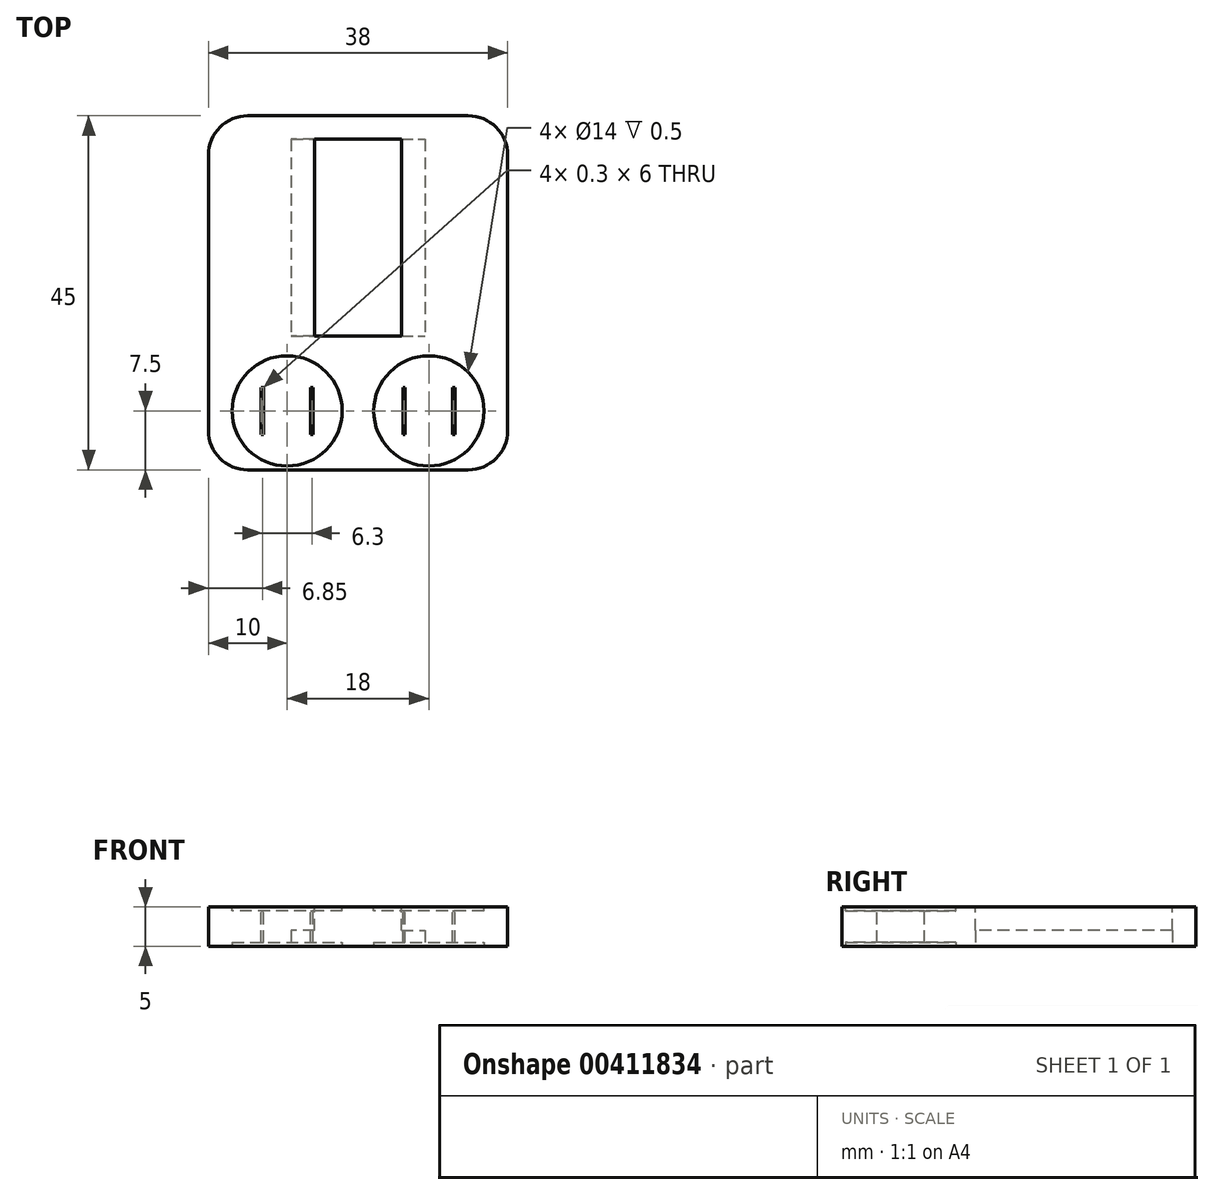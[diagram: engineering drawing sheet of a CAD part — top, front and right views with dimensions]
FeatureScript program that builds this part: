
annotation { "Feature Type Name" : "Feature", "Feature Type Description" : "" }
export const myFeature = defineFeature(function(context is Context, id is Id, definition is map)
    precondition{}
    {
        {
            var Q0;
            Q0=qCreatedBy(makeId("Top.planeOp"),FACE);
            var sketch = newSketch(context, id + "F0", { "sketchPlane" : qUnion([Q0])});
            skLineSegment(sketch, "E0.bottom", {"start": v(0, 0) * mm, "end": v(38, 0) * mm});
            skLineSegment(sketch, "E0.top", {"start": v(0, 45) * mm, "end": v(38, 45) * mm});
            skLineSegment(sketch, "E0.left", {"start": v(0, 0) * mm, "end": v(0, 45) * mm});
            skLineSegment(sketch, "E0.right", {"start": v(38, 0) * mm, "end": v(38, 45) * mm});
            skSolve(sketch);
        }
        {
            var Q0;
            Q0 = qSketchRegion(id + "F0", true);
            extrude(context, id + "F1", {"entities" : qUnion([Q0]), "depth" : 5 * mm});
        }
        {
            var Q0;
            Q0=makeQuery(id+"F1.opExtrude","CAP_FACE",FACE,{"disambiguationData":[OSD([sQuery(id+"F0.wireOp",EDGE,"E0.bottom"),sQuery(id+"F0.wireOp",EDGE,"E0.top"),sQuery(id+"F0.wireOp",EDGE,"E0.left"),sQuery(id+"F0.wireOp",EDGE,"E0.right")])],"isStart":false});
            var sketch = newSketch(context, id + "F2", { "sketchPlane" : qUnion([Q0])});
            skLineSegment(sketch, "E1.bottom", {"start": v(13.5, 42) * mm, "end": v(24.5, 42) * mm});
            skLineSegment(sketch, "E1.top", {"start": v(13.5, 17) * mm, "end": v(24.5, 17) * mm});
            skLineSegment(sketch, "E1.left", {"start": v(13.5, 42) * mm, "end": v(13.5, 17) * mm});
            skLineSegment(sketch, "E1.right", {"start": v(24.5, 42) * mm, "end": v(24.5, 17) * mm});
            skLineSegment(sketch, "E2", {"start": v(19, 45) * mm, "end": v(19, 0) * mm});
            skCircle(sketch, "E3", {"center": v(10, 7.5) * mm, "radius": 7 * mm});
            skCircle(sketch, "E4", {"center": v(28, 7.5) * mm, "radius": 7 * mm});
            skSolve(sketch);
        }
        {
            var Q0;
            Q0=makeQuery(id+"F2.imprint","IMPRINT",FACE,{"disambiguationData":[TD([[makeQuery(id+"F2.imprint","IMPRINT",EDGE,{"derivedFrom":sQuery(id+"F2.wireOp",EDGE,"E3")}),1.0]])]});
            var Q1;
            Q1=makeQuery(id+"F2.imprint","IMPRINT",FACE,{"disambiguationData":[TD([[makeQuery(id+"F2.imprint","IMPRINT",EDGE,{"derivedFrom":sQuery(id+"F2.wireOp",EDGE,"E4")}),1.0]])]});
            extrude(context, id + "F3", {"entities" : qUnion([Q0, Q1]), "operationType" : NewBodyOperationType.REMOVE, "oppositeDirection" : true, "depth" : 0.5 * mm});
        }
        {
            var Q0;
            {var subQ0=sQuery(id+"F2.wireOp",EDGE,"E1.left");Q0=makeQuery(id+"F2.imprint","IMPRINT",FACE,{"disambiguationData":[TD([[makeQuery(id+"F2.imprint","IMPRINT",EDGE,{"derivedFrom":subQ0}),1.0]])]});}
            var Q1;
            {var subQ0=sQuery(id+"F2.wireOp",EDGE,"E1.right");Q1=makeQuery(id+"F2.imprint","IMPRINT",FACE,{"disambiguationData":[TD([[makeQuery(id+"F2.imprint","IMPRINT",EDGE,{"derivedFrom":subQ0}),-1.0]])]});}
            extrude(context, id + "F4", {"entities" : qUnion([Q0, Q1]), "operationType" : NewBodyOperationType.REMOVE, "endBound" : BoundingType.THROUGH_ALL, "oppositeDirection" : true, "depth" : 25 * mm});
        }
        {
            var Q0;
            Q0=makeQuery(id+"F1.opExtrude","CAP_FACE",FACE,{"disambiguationData":[OSD([sQuery(id+"F0.wireOp",EDGE,"E0.bottom"),sQuery(id+"F0.wireOp",EDGE,"E0.top"),sQuery(id+"F0.wireOp",EDGE,"E0.left"),sQuery(id+"F0.wireOp",EDGE,"E0.right")])],"isStart":true});
            var sketch = newSketch(context, id + "F5", { "sketchPlane" : qUnion([Q0])});
            skLineSegment(sketch, "E5.bottom", {"start": v(24.5, -42) * mm, "end": v(27.5, -42) * mm});
            skLineSegment(sketch, "E5.top", {"start": v(24.5, -17) * mm, "end": v(27.5, -17) * mm});
            skLineSegment(sketch, "E5.left", {"start": v(24.5, -42) * mm, "end": v(24.5, -17) * mm});
            skLineSegment(sketch, "E5.right", {"start": v(27.5, -42) * mm, "end": v(27.5, -17) * mm});
            skLineSegment(sketch, "E6.bottom", {"start": v(13.5, -42) * mm, "end": v(10.5, -42) * mm});
            skLineSegment(sketch, "E6.top", {"start": v(13.5, -17) * mm, "end": v(10.5, -17) * mm});
            skLineSegment(sketch, "E6.left", {"start": v(13.5, -42) * mm, "end": v(13.5, -17) * mm});
            skLineSegment(sketch, "E6.right", {"start": v(10.5, -42) * mm, "end": v(10.5, -17) * mm});
            skSolve(sketch);
        }
        {
            var Q0;
            Q0 = qSketchRegion(id + "F5", true);
            extrude(context, id + "F6", {"entities" : qUnion([Q0]), "operationType" : NewBodyOperationType.REMOVE, "oppositeDirection" : true, "depth" : 2 * mm});
        }
        {
            var Q0;
            Q0=makeQuery(id+"F3.boolean.opBoolean","COPY",FACE,{"derivedFrom":makeQuery(id+"F3.opExtrude","CAP_FACE",FACE,{"disambiguationData":[OSD([sQuery(id+"F2.wireOp",EDGE,"E3")])],"isStart":false})});
            var sketch = newSketch(context, id + "F7", { "sketchPlane" : qUnion([Q0])});
            skLineSegment(sketch, "E7.bottom", {"start": v(6.7, 10.5) * mm, "end": v(7, 10.5) * mm});
            skLineSegment(sketch, "E7.top", {"start": v(6.7, 4.5) * mm, "end": v(7, 4.5) * mm});
            skLineSegment(sketch, "E7.left", {"start": v(6.7, 10.5) * mm, "end": v(6.7, 4.5) * mm});
            skLineSegment(sketch, "E7.right", {"start": v(7, 10.5) * mm, "end": v(7, 4.5) * mm});
            skLineSegment(sketch, "E8.bottom", {"start": v(13, 10.5) * mm, "end": v(13.3, 10.5) * mm});
            skLineSegment(sketch, "E8.top", {"start": v(13, 4.5) * mm, "end": v(13.3, 4.5) * mm});
            skLineSegment(sketch, "E8.left", {"start": v(13, 10.5) * mm, "end": v(13, 4.5) * mm});
            skLineSegment(sketch, "E8.right", {"start": v(13.3, 10.5) * mm, "end": v(13.3, 4.5) * mm});
            skLineSegment(sketch, "E9.bottom", {"start": v(24.7, 10.5) * mm, "end": v(25, 10.5) * mm});
            skLineSegment(sketch, "E9.top", {"start": v(24.7, 4.5) * mm, "end": v(25, 4.5) * mm});
            skLineSegment(sketch, "E9.left", {"start": v(24.7, 10.5) * mm, "end": v(24.7, 4.5) * mm});
            skLineSegment(sketch, "E9.right", {"start": v(25, 10.5) * mm, "end": v(25, 4.5) * mm});
            skLineSegment(sketch, "E10.bottom", {"start": v(31, 10.5) * mm, "end": v(31.3, 10.5) * mm});
            skLineSegment(sketch, "E10.top", {"start": v(31, 4.5) * mm, "end": v(31.3, 4.5) * mm});
            skLineSegment(sketch, "E10.left", {"start": v(31, 10.5) * mm, "end": v(31, 4.5) * mm});
            skLineSegment(sketch, "E10.right", {"start": v(31.3, 10.5) * mm, "end": v(31.3, 4.5) * mm});
            skSolve(sketch);
        }
        {
            var Q0;
            Q0 = qSketchRegion(id + "F7", true);
            extrude(context, id + "F8", {"entities" : qUnion([Q0]), "operationType" : NewBodyOperationType.REMOVE, "oppositeDirection" : true, "depth" : 5 * mm});
        }
        {
            var Q0;
            Q0=makeQuery(id+"F1.opExtrude","CAP_FACE",FACE,{"disambiguationData":[OSD([sQuery(id+"F0.wireOp",EDGE,"E0.bottom"),sQuery(id+"F0.wireOp",EDGE,"E0.top"),sQuery(id+"F0.wireOp",EDGE,"E0.left"),sQuery(id+"F0.wireOp",EDGE,"E0.right")])],"isStart":true});
            var sketch = newSketch(context, id + "F9", { "sketchPlane" : qUnion([Q0])});
            skCircle(sketch, "E11", {"center": v(28, -7.5) * mm, "radius": 7 * mm});
            skCircle(sketch, "E12", {"center": v(10, -7.5) * mm, "radius": 7 * mm});
            skSolve(sketch);
        }
        {
            var Q0;
            Q0 = qSketchRegion(id + "F9", true);
            extrude(context, id + "F10", {"entities" : qUnion([Q0]), "operationType" : NewBodyOperationType.REMOVE, "oppositeDirection" : true, "depth" : 0.5 * mm});
        }
        {
            var Q0;
            Q0=makeQuery(id+"F1.opExtrude","SWEPT_EDGE",EDGE,{"disambiguationData":[OSD([sQuery(id+"F0.wireOp",EDGE,"E0.bottom"),sQuery(id+"F0.wireOp",EDGE,"E0.left")])]});
            var Q1;
            Q1=makeQuery(id+"F1.opExtrude","SWEPT_EDGE",EDGE,{"disambiguationData":[OSD([sQuery(id+"F0.wireOp",EDGE,"E0.bottom"),sQuery(id+"F0.wireOp",EDGE,"E0.right")])]});
            var Q2;
            Q2=makeQuery(id+"F1.opExtrude","SWEPT_EDGE",EDGE,{"disambiguationData":[OSD([sQuery(id+"F0.wireOp",EDGE,"E0.top"),sQuery(id+"F0.wireOp",EDGE,"E0.right")])]});
            var Q3;
            Q3=makeQuery(id+"F1.opExtrude","SWEPT_EDGE",EDGE,{"disambiguationData":[OSD([sQuery(id+"F0.wireOp",EDGE,"E0.top"),sQuery(id+"F0.wireOp",EDGE,"E0.left")])]});
            fillet(context, id + "F11", {"entities" : qUnion([Q0, Q1, Q2, Q3]), "radius" : 5 * mm, "tangentPropagation" : true, "allowEdgeOverflow" : false});
        }
    });
